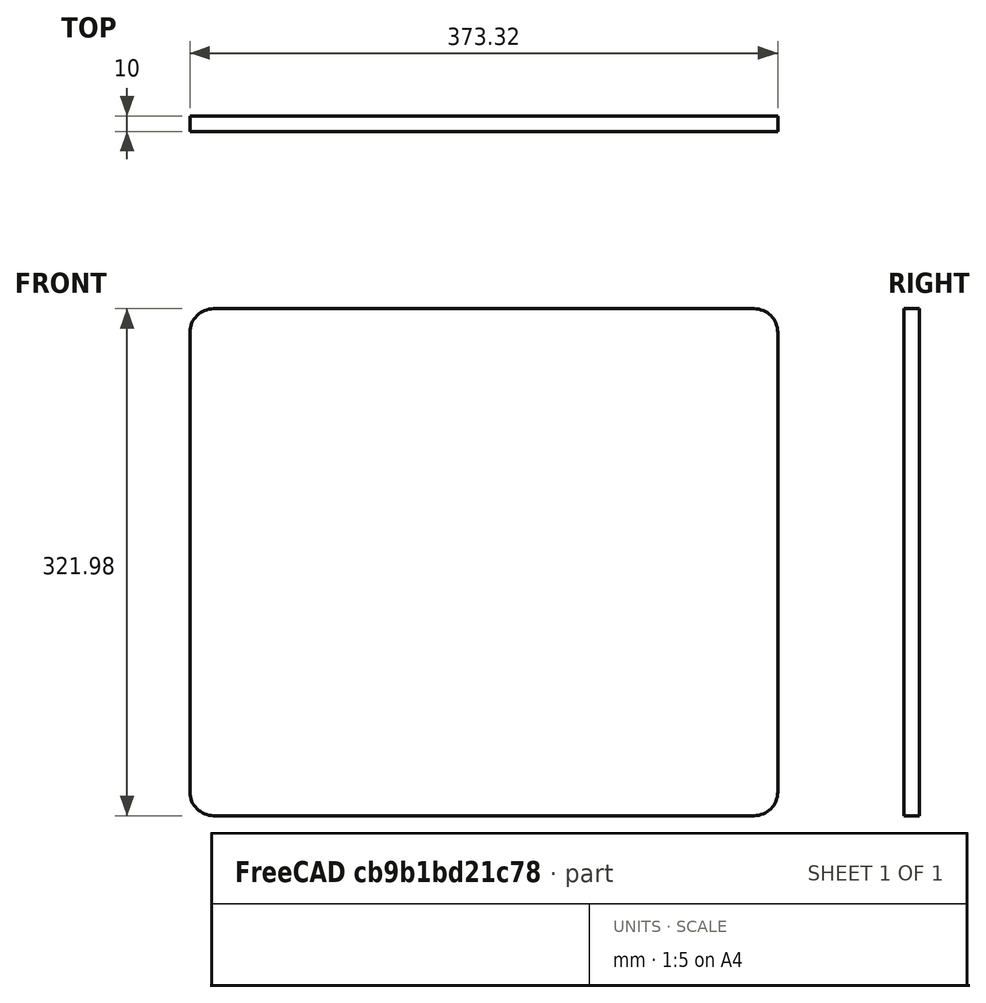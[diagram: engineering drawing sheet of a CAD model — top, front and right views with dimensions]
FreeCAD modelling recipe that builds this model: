
FCSTD DOCUMENT  (FreeCAD 0.16R6706 (Git))
Label: porte
License: All rights reserved
LicenseURL: http://en.wikipedia.org/wiki/All_rights_reserved
objects: Sketcher::SketchObject×1, PartDesign::Pad×1
note: 3 computed .brp shape members not serialized (recipe doc carries the construction recipe); baked Part::Feature solids carry a one-line shape summary decoded from their .brp

FEATURE [Sketcher::SketchObject] Sketch
  Placement = pos=(0,0,0) rot=(-1,0,0;4.71239rad)
  sketch-geometry (8):
    g0: LineSegment StartX=15.0462 StartY=0.0199586 StartZ=0 EndX=358.366 EndY=0.0199586 EndZ=0
    g1: LineSegment StartX=373.366 StartY=15.02 StartZ=0 EndX=373.366 EndY=307 EndZ=0
    g2: LineSegment StartX=358.366 StartY=322 StartZ=0 EndX=15.0462 EndY=322 EndZ=0
    g3: LineSegment StartX=0.0462156 StartY=307 StartZ=0 EndX=0.0462156 EndY=15.02 EndZ=0
    g4: ArcOfCircle CenterX=15.0462 CenterY=307 CenterZ=0 NormalX=0 NormalY=0 NormalZ=1 Radius=15 StartAngle=1.5708 EndAngle=3.14159
    g5: ArcOfCircle CenterX=358.366 CenterY=307 CenterZ=0 NormalX=0 NormalY=0 NormalZ=1 Radius=15 StartAngle=0 EndAngle=1.5708
    g6: ArcOfCircle CenterX=358.366 CenterY=15.02 CenterZ=0 NormalX=0 NormalY=0 NormalZ=1 Radius=15 StartAngle=4.71239 EndAngle=6.28319
    g7: ArcOfCircle CenterX=15.0462 CenterY=15.02 CenterZ=0 NormalX=0 NormalY=0 NormalZ=1 Radius=15 StartAngle=3.14159 EndAngle=4.71239
  constraints (18):
    c: Horizontal(g0)
    c: Horizontal(g2)
    c: Vertical(g1)
    c: Vertical(g3)
    c: Tangent(g2,g4) = -1.5708
    c: Tangent(g3,g4) = -1.5708
    c: Tangent(g1,g5) = -1.5708
    c: Tangent(g2,g5) = -1.5708
    c: Tangent(g0,g6) = -1.5708
    c: Tangent(g1,g6) = -1.5708
    c: Tangent(g0,g7) = -1.5708
    c: Tangent(g3,g7) = -1.5708
    c: DistanceX(g3,g1) = 373.32
    c: DistanceY(g0,g2) = 321.98
    c: Equal(g7,g4)
    c: Equal(g4,g5)
    c: Equal(g5,g6)
    c: Radius(g5) = 15
FEATURE [PartDesign::Pad] Pad
  Length = 10
  Length2 = 100
  Placement = pos=(0,0,0) rot=(-1,0,0;4.71239rad)
  Sketch = -> Sketch
  Type = 0
